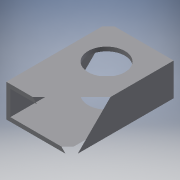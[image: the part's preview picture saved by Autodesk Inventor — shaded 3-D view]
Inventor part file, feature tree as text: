
AUTODESK INVENTOR PART (.ipt)
format: ipt  version: 2016 (Build 200138000, 138)  size: 105,472 bytes
history: native  units: in
note: dims shown in document units (in); Inventor stores cm internally (conversion verified against a paired STEP export)
features: extrude x2, sketch x2
ambient origin geometry x8: Origin, YZ Plane, XZ Plane, XY Plane, X Axis, Y Axis, Z Axis, Center Point
bodies: Solid1 (feature_tree)
feature tree (4):
  extrude  "Extrusion1"  Depth=1.0in
  extrude  "Extrusion2"  Depth=3.125in TaperAngle=0.0deg
  sketch  "Sketch1"  dims[d0=3.0in d1=1.0in]
  sketch  "Sketch2"  dims[d2=0.125in d3=3.125in d4=0.0in d5=1.125in d6=1.5in d7=1.394in d8=1.0in d9=0.0in]
